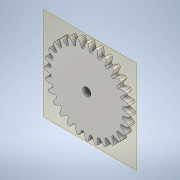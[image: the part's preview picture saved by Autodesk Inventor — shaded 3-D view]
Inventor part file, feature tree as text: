
AUTODESK INVENTOR PART (.ipt)
format: ipt  version: 2022 (Build 260153000, 153)  size: 259,072 bytes
history: native  units: mm (DEFAULTED — no unit token found)
features: plane x4, other x3, sketch x2, extrude x1
ambient origin geometry x8: Origin, YZ Plane, XZ Plane, XY Plane, X Axis, Y Axis, Z Axis, Center Point
bodies: Solid1 (feature_tree)
feature tree (10):
  extrude  "Extrusion1"  Depth=5.0mm TaperAngle=0.0deg
  plane  "Work Plane2"
  plane  "Work Plane8"
  plane  "Work Plane9"
  other  "Spur Gear"
  plane  "Work Plane11"
  sketch  "Sketch1"  dims[d0=67.41388mm d1=5.0mm d2=0.0mm]
  sketch  "Sketch2"  dims[d3=63.0mm d4=10.0mm d5=0.0mm d16=65.0mm d17=0.0mm d34=1.121997mm d39=0.0mm d41=0.0mm d43=65.0mm d46=65.0mm d47=0.0mm d48=0.0mm d49=6.5mm]
  other  "Srf1"
  other  "Pitch Diameter"
